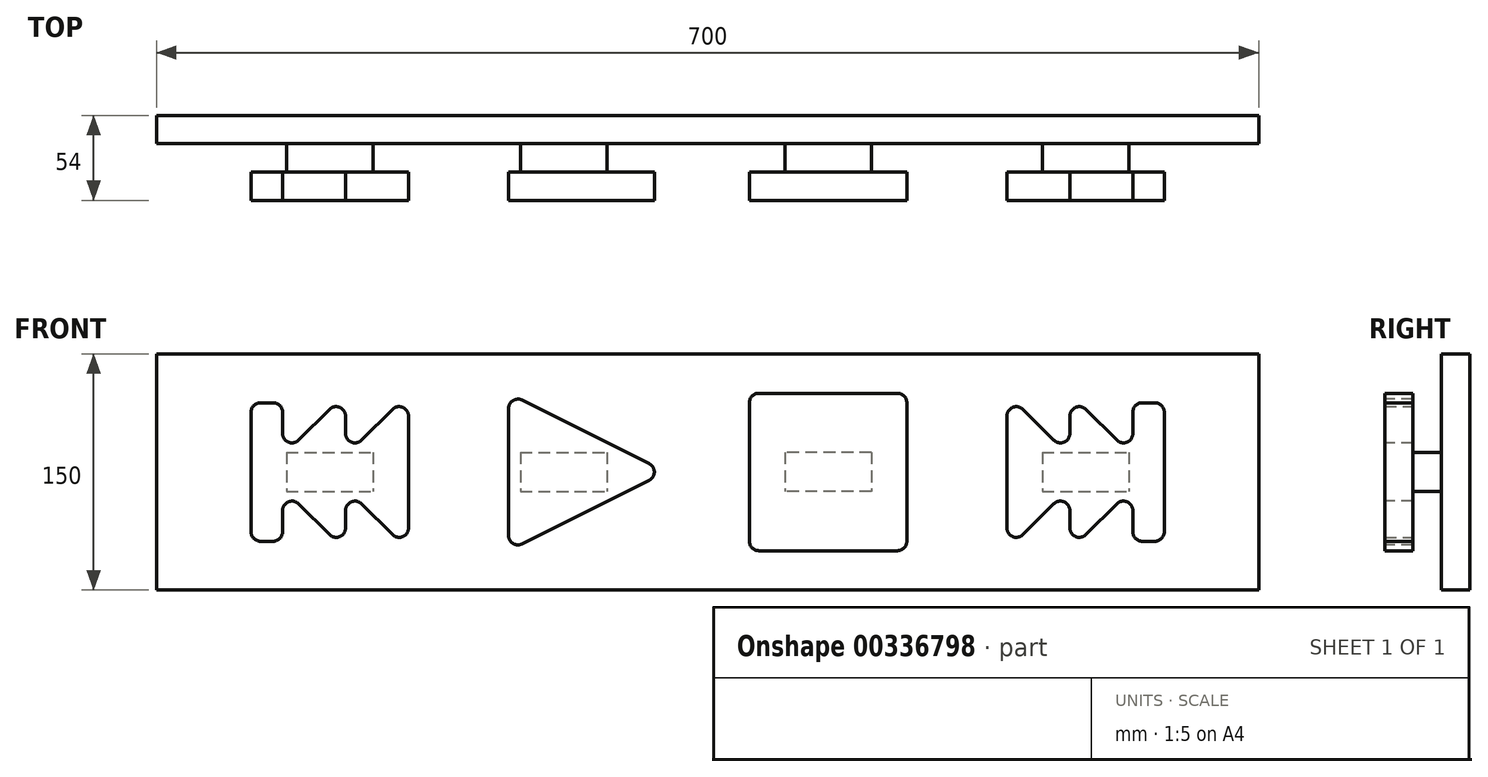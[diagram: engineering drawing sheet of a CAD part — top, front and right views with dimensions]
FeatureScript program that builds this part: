
annotation { "Feature Type Name" : "Feature", "Feature Type Description" : "" }
export const myFeature = defineFeature(function(context is Context, id is Id, definition is map)
    precondition{}
    {
        {
            var Q0;
            Q0=qCreatedBy(makeId("Front.planeOp"),FACE);
            var sketch = newSketch(context, id + "F0", { "sketchPlane" : qUnion([Q0])});
            skLineSegment(sketch, "E0.bottom", {"start": v(350, 75) * mm, "end": v(-350, 75) * mm});
            skLineSegment(sketch, "E0.top", {"start": v(350, -75) * mm, "end": v(-350, -75) * mm});
            skLineSegment(sketch, "E0.left", {"start": v(350, 75) * mm, "end": v(350, -75) * mm});
            skLineSegment(sketch, "E0.right", {"start": v(-350, 75) * mm, "end": v(-350, -75) * mm});
            skPoint(sketch, "E0.middle", {"position": v(0, 0) * mm});
            skSolve(sketch);
        }
        {
            var Q0;
            Q0=makeQuery(id+"F0.imprint","IMPRINT",FACE,{"disambiguationData":[TD([[makeQuery(id+"F0.imprint","IMPRINT",EDGE,{"derivedFrom":sQuery(id+"F0.wireOp",EDGE,"E0.bottom")}),1.0]])]});
            extrude(context, id + "F1", {"entities" : qUnion([Q0]), "depth" : 18 * mm});
        }
        {
            var Q0;
            Q0=makeQuery(id+"F1.opExtrude","CAP_FACE",FACE,{"disambiguationData":[OSD([sQuery(id+"F0.wireOp",EDGE,"E0.bottom"),sQuery(id+"F0.wireOp",EDGE,"E0.top"),sQuery(id+"F0.wireOp",EDGE,"E0.left"),sQuery(id+"F0.wireOp",EDGE,"E0.right")])],"isStart":false});
            var sketch = newSketch(context, id + "F2", { "sketchPlane" : qUnion([Q0])});
            skLineSegment(sketch, "E1.left", {"start": v(50, 50) * mm, "end": v(50, -50) * mm, "construction": true});
            skPoint(sketch, "E1.middle", {"position": v(0, 0) * mm});
            skLineSegment(sketch, "E2", {"start": v(-50, 0) * mm, "end": v(50, 0) * mm, "construction": true});
            skPoint(sketch, "E3", {"position": v(10, 10) * mm});
            skPoint(sketch, "E4", {"position": v(10, -10) * mm});
            skPoint(sketch, "E5", {"position": v(-30, 10) * mm});
            skPoint(sketch, "E6", {"position": v(-30, -10) * mm});
            skLineSegment(sketch, "E7", {"start": v(-50, 44) * mm, "end": v(-50, -44) * mm});
            skLineSegment(sketch, "E8", {"start": v(-30, -44) * mm, "end": v(-30, -10) * mm});
            skLineSegment(sketch, "E9", {"start": v(-30, -10) * mm, "end": v(10, -50) * mm});
            skLineSegment(sketch, "E10", {"start": v(10, -50) * mm, "end": v(10, -10) * mm});
            skLineSegment(sketch, "E11", {"start": v(10, -10) * mm, "end": v(50, -50) * mm});
            skLineSegment(sketch, "E12", {"start": v(50, -50) * mm, "end": v(50, 50) * mm});
            skLineSegment(sketch, "E13", {"start": v(50, 50) * mm, "end": v(10, 10) * mm});
            skLineSegment(sketch, "E14", {"start": v(10, 10) * mm, "end": v(10, 50) * mm});
            skLineSegment(sketch, "E15", {"start": v(10, 50) * mm, "end": v(-30, 10) * mm});
            skLineSegment(sketch, "E16", {"start": v(-30, 10) * mm, "end": v(-30, 44) * mm});
            skLineSegment(sketch, "E17", {"start": v(-50, 44) * mm, "end": v(-30, 44) * mm});
            skLineSegment(sketch, "E18", {"start": v(-50, -44) * mm, "end": v(-30, -44) * mm});
            skPoint(sketch, "E19.orphan", {"position": v(-50, 50) * mm});
            skPoint(sketch, "E20.orphan", {"position": v(-50, -50) * mm});
            skSolve(sketch);
        }
        {
            var Q0;
            Q0 = qSketchRegion(id + "F2", true);
            extrude(context, id + "F3", {"entities" : qUnion([Q0]), "depth" : 18 * mm});
        }
        {
            var Q0;
            Q0=makeQuery(id+"F1.opExtrude","CAP_FACE",FACE,{"disambiguationData":[OSD([sQuery(id+"F0.wireOp",EDGE,"E0.bottom"),sQuery(id+"F0.wireOp",EDGE,"E0.top"),sQuery(id+"F0.wireOp",EDGE,"E0.left"),sQuery(id+"F0.wireOp",EDGE,"E0.right")])],"isStart":false});
            var sketch = newSketch(context, id + "F4", { "sketchPlane" : qUnion([Q0])});
            skLineSegment(sketch, "E21.right", {"start": v(-50, 50) * mm, "end": v(-50, -50) * mm});
            skPoint(sketch, "E21.middle", {"position": v(0, 0) * mm});
            skLineSegment(sketch, "E22", {"start": v(-50, 50) * mm, "end": v(50, 0) * mm});
            skLineSegment(sketch, "E23", {"start": v(50, 0) * mm, "end": v(-50, -50) * mm});
            skSolve(sketch);
        }
        {
            var Q0;
            Q0=makeQuery(id+"F4.imprint","IMPRINT",FACE,{"disambiguationData":[TD([[makeQuery(id+"F4.imprint","IMPRINT",EDGE,{"derivedFrom":sQuery(id+"F4.wireOp",EDGE,"E21.right")}),1.0]])]});
            extrude(context, id + "F5", {"entities" : qUnion([Q0]), "depth" : 18 * mm});
        }
        {
            var Q0;
            Q0=makeQuery(id+"F1.opExtrude","CAP_FACE",FACE,{"disambiguationData":[OSD([sQuery(id+"F0.wireOp",EDGE,"E0.bottom"),sQuery(id+"F0.wireOp",EDGE,"E0.top"),sQuery(id+"F0.wireOp",EDGE,"E0.left"),sQuery(id+"F0.wireOp",EDGE,"E0.right")])],"isStart":false});
            var sketch = newSketch(context, id + "F6", { "sketchPlane" : qUnion([Q0])});
            skLineSegment(sketch, "E24.bottom", {"start": v(50, 50) * mm, "end": v(-50, 50) * mm});
            skLineSegment(sketch, "E24.top", {"start": v(50, -50) * mm, "end": v(-50, -50) * mm});
            skLineSegment(sketch, "E24.left", {"start": v(50, 50) * mm, "end": v(50, -50) * mm});
            skLineSegment(sketch, "E24.right", {"start": v(-50, 50) * mm, "end": v(-50, -50) * mm});
            skPoint(sketch, "E24.middle", {"position": v(0, 0) * mm});
            skSolve(sketch);
        }
        {
            var Q0;
            Q0=makeQuery(id+"F6.imprint","IMPRINT",FACE,{"disambiguationData":[TD([[makeQuery(id+"F6.imprint","IMPRINT",EDGE,{"derivedFrom":sQuery(id+"F6.wireOp",EDGE,"E24.bottom")}),1.0]])]});
            extrude(context, id + "F7", {"entities" : qUnion([Q0]), "depth" : 18 * mm});
        }
        {
            var Q0;
            Q0=makeQuery(id+"F1.opExtrude","CAP_FACE",FACE,{"disambiguationData":[OSD([sQuery(id+"F0.wireOp",EDGE,"E0.bottom"),sQuery(id+"F0.wireOp",EDGE,"E0.top"),sQuery(id+"F0.wireOp",EDGE,"E0.left"),sQuery(id+"F0.wireOp",EDGE,"E0.right")])],"isStart":false});
            var sketch = newSketch(context, id + "F8", { "sketchPlane" : qUnion([Q0])});
            skLineSegment(sketch, "E25.left", {"start": v(-50, -50) * mm, "end": v(-50, 50) * mm, "construction": true});
            skPoint(sketch, "E25.middle", {"position": v(0, 0) * mm});
            skLineSegment(sketch, "E26", {"start": v(50, 0) * mm, "end": v(-50, 0) * mm, "construction": true});
            skPoint(sketch, "E27", {"position": v(-10, -10) * mm});
            skPoint(sketch, "E28", {"position": v(-10, 10) * mm});
            skPoint(sketch, "E29", {"position": v(30, -10) * mm});
            skPoint(sketch, "E30", {"position": v(30, 10) * mm});
            skLineSegment(sketch, "E31", {"start": v(50, -44) * mm, "end": v(50, 44) * mm});
            skLineSegment(sketch, "E32", {"start": v(30, 44) * mm, "end": v(30, 10) * mm});
            skLineSegment(sketch, "E33", {"start": v(30, 10) * mm, "end": v(-10, 50) * mm});
            skLineSegment(sketch, "E34", {"start": v(-10, 50) * mm, "end": v(-10, 10) * mm});
            skLineSegment(sketch, "E35", {"start": v(-10, 10) * mm, "end": v(-50, 50) * mm});
            skLineSegment(sketch, "E36", {"start": v(-50, 50) * mm, "end": v(-50, -50) * mm});
            skLineSegment(sketch, "E37", {"start": v(-50, -50) * mm, "end": v(-10, -10) * mm});
            skLineSegment(sketch, "E38", {"start": v(-10, -10) * mm, "end": v(-10, -50) * mm});
            skLineSegment(sketch, "E39", {"start": v(-10, -50) * mm, "end": v(30, -10) * mm});
            skLineSegment(sketch, "E40", {"start": v(30, -10) * mm, "end": v(30, -44) * mm});
            skLineSegment(sketch, "E41", {"start": v(30, 44) * mm, "end": v(50, 44) * mm});
            skLineSegment(sketch, "E42", {"start": v(30, -44) * mm, "end": v(50, -44) * mm});
            skPoint(sketch, "E43.orphan", {"position": v(50, 50) * mm});
            skPoint(sketch, "E44.end.orphan", {"position": v(50, -50) * mm});
            skSolve(sketch);
        }
        {
            var Q0;
            Q0=makeQuery(id+"F8.imprint","IMPRINT",FACE,{"disambiguationData":[TD([[makeQuery(id+"F8.imprint","IMPRINT",EDGE,{"derivedFrom":sQuery(id+"F8.wireOp",EDGE,"E31")}),1.0]])]});
            extrude(context, id + "F9", {"entities" : qUnion([Q0]), "depth" : 18 * mm});
        }
        {
            var Q0;
            Q0=makeQuery(id+"F3.opExtrude","SWEPT_EDGE",EDGE,{"disambiguationData":[OSD([sQuery(id+"F2.wireOp",EDGE,"jNEnzam2-YLTJ-LkkW-kFy7-VWHj9kg6MtIO"),sQuery(id+"F2.wireOp",EDGE,"E7")])]});
            var Q1;
            Q1=makeQuery(id+"F3.opExtrude","SWEPT_EDGE",EDGE,{"disambiguationData":[OSD([sQuery(id+"F2.wireOp",EDGE,"jNEnzam2-YLTJ-LkkW-kFy7-VWHj9kg6MtIO"),sQuery(id+"F2.wireOp",EDGE,"E16")])]});
            var Q2;
            Q2=makeQuery(id+"F3.opExtrude","SWEPT_EDGE",EDGE,{"disambiguationData":[OSD([sQuery(id+"F2.wireOp",EDGE,"E14"),sQuery(id+"F2.wireOp",EDGE,"E15")])]});
            var Q3;
            Q3=makeQuery(id+"F3.opExtrude","SWEPT_EDGE",EDGE,{"disambiguationData":[OSD([sQuery(id+"F2.wireOp",EDGE,"E12"),sQuery(id+"F2.wireOp",EDGE,"E13")])]});
            var Q4;
            Q4=makeQuery(id+"F5.opExtrude","SWEPT_EDGE",EDGE,{"disambiguationData":[OSD([sQuery(id+"F4.wireOp",EDGE,"E21.right"),sQuery(id+"F4.wireOp",EDGE,"E22")])]});
            var Q5;
            Q5=makeQuery(id+"F7.opExtrude","SWEPT_EDGE",EDGE,{"disambiguationData":[OSD([sQuery(id+"F6.wireOp",EDGE,"E24.bottom"),sQuery(id+"F6.wireOp",EDGE,"E24.right")])]});
            var Q6;
            Q6=makeQuery(id+"F7.opExtrude","SWEPT_EDGE",EDGE,{"disambiguationData":[OSD([sQuery(id+"F6.wireOp",EDGE,"E24.bottom"),sQuery(id+"F6.wireOp",EDGE,"E24.left")])]});
            var Q7;
            Q7=makeQuery(id+"F3.opExtrude","SWEPT_EDGE",EDGE,{"disambiguationData":[OSD([sQuery(id+"F2.wireOp",EDGE,"E15"),sQuery(id+"F2.wireOp",EDGE,"E16")])]});
            var Q8;
            Q8=makeQuery(id+"F3.opExtrude","SWEPT_EDGE",EDGE,{"disambiguationData":[OSD([sQuery(id+"F2.wireOp",EDGE,"E13"),sQuery(id+"F2.wireOp",EDGE,"E14")])]});
            var Q9;
            Q9=makeQuery(id+"F7.opExtrude","SWEPT_EDGE",EDGE,{"disambiguationData":[OSD([sQuery(id+"F6.wireOp",EDGE,"E24.top"),sQuery(id+"F6.wireOp",EDGE,"E24.left")])]});
            var Q10;
            Q10=makeQuery(id+"F7.opExtrude","SWEPT_EDGE",EDGE,{"disambiguationData":[OSD([sQuery(id+"F6.wireOp",EDGE,"E24.top"),sQuery(id+"F6.wireOp",EDGE,"E24.right")])]});
            var Q11;
            Q11=makeQuery(id+"F5.opExtrude","SWEPT_EDGE",EDGE,{"disambiguationData":[OSD([sQuery(id+"F4.wireOp",EDGE,"E22"),sQuery(id+"F4.wireOp",EDGE,"E23")])]});
            var Q12;
            Q12=makeQuery(id+"F5.opExtrude","SWEPT_EDGE",EDGE,{"disambiguationData":[OSD([sQuery(id+"F4.wireOp",EDGE,"E21.right"),sQuery(id+"F4.wireOp",EDGE,"E23")])]});
            var Q13;
            Q13=makeQuery(id+"F3.opExtrude","SWEPT_EDGE",EDGE,{"disambiguationData":[OSD([sQuery(id+"F2.wireOp",EDGE,"E11"),sQuery(id+"F2.wireOp",EDGE,"E12")])]});
            var Q14;
            Q14=makeQuery(id+"F3.opExtrude","SWEPT_EDGE",EDGE,{"disambiguationData":[OSD([sQuery(id+"F2.wireOp",EDGE,"E9"),sQuery(id+"F2.wireOp",EDGE,"E10")])]});
            var Q15;
            Q15=makeQuery(id+"F3.opExtrude","SWEPT_EDGE",EDGE,{"disambiguationData":[OSD([sQuery(id+"F2.wireOp",EDGE,"ZUAhIKnp-DANw-6E52-ARa7-giLd2jf8w72K"),sQuery(id+"F2.wireOp",EDGE,"E8")])]});
            var Q16;
            Q16=makeQuery(id+"F3.opExtrude","SWEPT_EDGE",EDGE,{"disambiguationData":[OSD([sQuery(id+"F2.wireOp",EDGE,"E7"),sQuery(id+"F2.wireOp",EDGE,"ZUAhIKnp-DANw-6E52-ARa7-giLd2jf8w72K")])]});
            var Q17;
            Q17=makeQuery(id+"F3.opExtrude","SWEPT_EDGE",EDGE,{"disambiguationData":[OSD([sQuery(id+"F2.wireOp",EDGE,"E10"),sQuery(id+"F2.wireOp",EDGE,"E11")])]});
            var Q18;
            Q18=makeQuery(id+"F3.opExtrude","SWEPT_EDGE",EDGE,{"disambiguationData":[OSD([sQuery(id+"F2.wireOp",EDGE,"E8"),sQuery(id+"F2.wireOp",EDGE,"E9")])]});
            var Q19;
            Q19=makeQuery(id+"F9.opExtrude","SWEPT_EDGE",EDGE,{"disambiguationData":[OSD([sQuery(id+"F8.wireOp",EDGE,"E32"),sQuery(id+"F8.wireOp",EDGE,"E41")])]});
            var Q20;
            Q20=makeQuery(id+"F9.opExtrude","SWEPT_EDGE",EDGE,{"disambiguationData":[OSD([sQuery(id+"F8.wireOp",EDGE,"E31"),sQuery(id+"F8.wireOp",EDGE,"E41")])]});
            var Q21;
            Q21=makeQuery(id+"F9.opExtrude","SWEPT_EDGE",EDGE,{"disambiguationData":[OSD([sQuery(id+"F8.wireOp",EDGE,"E31"),sQuery(id+"F8.wireOp",EDGE,"E42")])]});
            var Q22;
            Q22=makeQuery(id+"F9.opExtrude","SWEPT_EDGE",EDGE,{"disambiguationData":[OSD([sQuery(id+"F8.wireOp",EDGE,"E40"),sQuery(id+"F8.wireOp",EDGE,"E42")])]});
            var Q23;
            Q23=makeQuery(id+"F9.opExtrude","SWEPT_EDGE",EDGE,{"disambiguationData":[OSD([sQuery(id+"F8.wireOp",EDGE,"E33"),sQuery(id+"F8.wireOp",EDGE,"E34")])]});
            var Q24;
            Q24=makeQuery(id+"F9.opExtrude","SWEPT_EDGE",EDGE,{"disambiguationData":[OSD([sQuery(id+"F8.wireOp",EDGE,"E35"),sQuery(id+"F8.wireOp",EDGE,"E36")])]});
            var Q25;
            Q25=makeQuery(id+"F9.opExtrude","SWEPT_EDGE",EDGE,{"disambiguationData":[OSD([sQuery(id+"F8.wireOp",EDGE,"E38"),sQuery(id+"F8.wireOp",EDGE,"E39")])]});
            var Q26;
            Q26=makeQuery(id+"F9.opExtrude","SWEPT_EDGE",EDGE,{"disambiguationData":[OSD([sQuery(id+"F8.wireOp",EDGE,"E36"),sQuery(id+"F8.wireOp",EDGE,"E37")])]});
            var Q27;
            Q27=makeQuery(id+"F9.opExtrude","SWEPT_EDGE",EDGE,{"disambiguationData":[OSD([sQuery(id+"F8.wireOp",EDGE,"E34"),sQuery(id+"F8.wireOp",EDGE,"E35")])]});
            var Q28;
            Q28=makeQuery(id+"F9.opExtrude","SWEPT_EDGE",EDGE,{"disambiguationData":[OSD([sQuery(id+"F8.wireOp",EDGE,"E32"),sQuery(id+"F8.wireOp",EDGE,"E33")])]});
            var Q29;
            Q29=makeQuery(id+"F9.opExtrude","SWEPT_EDGE",EDGE,{"disambiguationData":[OSD([sQuery(id+"F8.wireOp",EDGE,"E39"),sQuery(id+"F8.wireOp",EDGE,"E40")])]});
            var Q30;
            Q30=makeQuery(id+"F9.opExtrude","SWEPT_EDGE",EDGE,{"disambiguationData":[OSD([sQuery(id+"F8.wireOp",EDGE,"E37"),sQuery(id+"F8.wireOp",EDGE,"E38")])]});
            fillet(context, id + "F10", {"entities" : qUnion([Q0, Q1, Q2, Q3, Q4, Q5, Q6, Q7, Q8, Q9, Q10, Q11, Q12, Q13, Q14, Q15, Q16, Q17, Q18, Q19, Q20, Q21, Q22, Q23, Q24, Q25, Q26, Q27, Q28, Q29, Q30]), "radius" : 6 * mm, "tangentPropagation" : true, "allowEdgeOverflow" : false});
        }
        {
            var Q0;
            Q0=makeQuery(id+"F3.opExtrude","SWEPT_BODY",BODY,{"disambiguationData":[OSD([sQuery(id+"F2.wireOp",EDGE,"E7"),sQuery(id+"F2.wireOp",EDGE,"E8"),sQuery(id+"F2.wireOp",EDGE,"E9"),sQuery(id+"F2.wireOp",EDGE,"E10"),sQuery(id+"F2.wireOp",EDGE,"E11"),sQuery(id+"F2.wireOp",EDGE,"E12"),sQuery(id+"F2.wireOp",EDGE,"E13"),sQuery(id+"F2.wireOp",EDGE,"E14"),sQuery(id+"F2.wireOp",EDGE,"E15"),sQuery(id+"F2.wireOp",EDGE,"E16"),sQuery(id+"F2.wireOp",EDGE,"E17"),sQuery(id+"F2.wireOp",EDGE,"E18")])]});
            transform(context, id + "F11", {"entities" : qUnion([Q0]), "transformType" : TransformType.TRANSLATION_3D, "dx" : -240 * mm, "dy" : 0 * mm, "dz" : 0 * mm, "makeCopy" : false});
        }
        {
            var Q0;
            Q0=makeQuery(id+"F5.opExtrude","SWEPT_BODY",BODY,{"disambiguationData":[OSD([sQuery(id+"F4.wireOp",EDGE,"E21.right"),sQuery(id+"F4.wireOp",EDGE,"E22"),sQuery(id+"F4.wireOp",EDGE,"E23")])]});
            transform(context, id + "F12", {"entities" : qUnion([Q0]), "transformType" : TransformType.TRANSLATION_3D, "dx" : -80 * mm, "dy" : 0 * mm, "dz" : 0 * mm, "makeCopy" : false});
        }
        {
            var Q0;
            Q0=makeQuery(id+"F9.opExtrude","SWEPT_BODY",BODY,{"disambiguationData":[OSD([sQuery(id+"F8.wireOp",EDGE,"E31"),sQuery(id+"F8.wireOp",EDGE,"E32"),sQuery(id+"F8.wireOp",EDGE,"E33"),sQuery(id+"F8.wireOp",EDGE,"E34"),sQuery(id+"F8.wireOp",EDGE,"E35"),sQuery(id+"F8.wireOp",EDGE,"E36"),sQuery(id+"F8.wireOp",EDGE,"E37"),sQuery(id+"F8.wireOp",EDGE,"E38"),sQuery(id+"F8.wireOp",EDGE,"E39"),sQuery(id+"F8.wireOp",EDGE,"E40"),sQuery(id+"F8.wireOp",EDGE,"E41"),sQuery(id+"F8.wireOp",EDGE,"E42")])]});
            transform(context, id + "F13", {"entities" : qUnion([Q0]), "transformType" : TransformType.TRANSLATION_3D, "dx" : 240 * mm, "dy" : 0 * mm, "dz" : 0 * mm, "makeCopy" : false});
        }
        {
            var Q0;
            Q0=makeQuery(id+"F7.opExtrude","SWEPT_BODY",BODY,{"disambiguationData":[OSD([sQuery(id+"F6.wireOp",EDGE,"E24.bottom"),sQuery(id+"F6.wireOp",EDGE,"E24.top"),sQuery(id+"F6.wireOp",EDGE,"E24.left"),sQuery(id+"F6.wireOp",EDGE,"E24.right")])]});
            transform(context, id + "F14", {"entities" : qUnion([Q0]), "transformType" : TransformType.TRANSLATION_3D, "dx" : 80 * mm, "dy" : 0 * mm, "dz" : 0 * mm, "makeCopy" : false});
        }
        {
            var Q0;
            Q0=makeQuery(id+"F7.opExtrude","SWEPT_BODY",BODY,{"disambiguationData":[OSD([sQuery(id+"F6.wireOp",EDGE,"E24.bottom"),sQuery(id+"F6.wireOp",EDGE,"E24.top"),sQuery(id+"F6.wireOp",EDGE,"E24.left"),sQuery(id+"F6.wireOp",EDGE,"E24.right")])]});
            transform(context, id + "F15", {"entities" : qUnion([Q0]), "transformType" : TransformType.TRANSLATION_3D, "dx" : -3.5 * mm, "dy" : 0 * mm, "dz" : 0 * mm, "makeCopy" : false});
        }
        {
            var Q0;
            Q0=makeQuery(id+"F5.opExtrude","SWEPT_BODY",BODY,{"disambiguationData":[OSD([sQuery(id+"F4.wireOp",EDGE,"E21.right"),sQuery(id+"F4.wireOp",EDGE,"E22"),sQuery(id+"F4.wireOp",EDGE,"E23")])]});
            transform(context, id + "F16", {"entities" : qUnion([Q0]), "transformType" : TransformType.TRANSLATION_3D, "dx" : 3.5 * mm, "dy" : 0 * mm, "dz" : 0 * mm, "makeCopy" : false});
        }
        {
            var Q0;
            Q0=makeQuery(id+"F3.opExtrude","SWEPT_BODY",BODY,{"disambiguationData":[OSD([sQuery(id+"F2.wireOp",EDGE,"E7"),sQuery(id+"F2.wireOp",EDGE,"E8"),sQuery(id+"F2.wireOp",EDGE,"E9"),sQuery(id+"F2.wireOp",EDGE,"E10"),sQuery(id+"F2.wireOp",EDGE,"E11"),sQuery(id+"F2.wireOp",EDGE,"E12"),sQuery(id+"F2.wireOp",EDGE,"E13"),sQuery(id+"F2.wireOp",EDGE,"E14"),sQuery(id+"F2.wireOp",EDGE,"E15"),sQuery(id+"F2.wireOp",EDGE,"E16"),sQuery(id+"F2.wireOp",EDGE,"E17"),sQuery(id+"F2.wireOp",EDGE,"E18")])]});
            var Q1;
            Q1=makeQuery(id+"F5.opExtrude","SWEPT_BODY",BODY,{"disambiguationData":[OSD([sQuery(id+"F4.wireOp",EDGE,"E21.right"),sQuery(id+"F4.wireOp",EDGE,"E22"),sQuery(id+"F4.wireOp",EDGE,"E23")])]});
            var Q2;
            Q2=makeQuery(id+"F7.opExtrude","SWEPT_BODY",BODY,{"disambiguationData":[OSD([sQuery(id+"F6.wireOp",EDGE,"E24.bottom"),sQuery(id+"F6.wireOp",EDGE,"E24.top"),sQuery(id+"F6.wireOp",EDGE,"E24.left"),sQuery(id+"F6.wireOp",EDGE,"E24.right")])]});
            var Q3;
            Q3=makeQuery(id+"F9.opExtrude","SWEPT_BODY",BODY,{"disambiguationData":[OSD([sQuery(id+"F8.wireOp",EDGE,"E31"),sQuery(id+"F8.wireOp",EDGE,"E32"),sQuery(id+"F8.wireOp",EDGE,"E33"),sQuery(id+"F8.wireOp",EDGE,"E34"),sQuery(id+"F8.wireOp",EDGE,"E35"),sQuery(id+"F8.wireOp",EDGE,"E36"),sQuery(id+"F8.wireOp",EDGE,"E37"),sQuery(id+"F8.wireOp",EDGE,"E38"),sQuery(id+"F8.wireOp",EDGE,"E39"),sQuery(id+"F8.wireOp",EDGE,"E40"),sQuery(id+"F8.wireOp",EDGE,"E41"),sQuery(id+"F8.wireOp",EDGE,"E42")])]});
            transform(context, id + "F17", {"entities" : qUnion([Q0, Q1, Q2, Q3]), "transformType" : TransformType.TRANSLATION_3D, "dx" : 0 * mm, "dy" : -18 * mm, "dz" : 0 * mm, "makeCopy" : false});
        }
        {
            var Q0;
            Q0=makeQuery(id+"F1.opExtrude","CAP_FACE",FACE,{"disambiguationData":[OSD([sQuery(id+"F0.wireOp",EDGE,"E0.bottom"),sQuery(id+"F0.wireOp",EDGE,"E0.top"),sQuery(id+"F0.wireOp",EDGE,"E0.left"),sQuery(id+"F0.wireOp",EDGE,"E0.right")])],"isStart":false});
            var sketch = newSketch(context, id + "F18", { "sketchPlane" : qUnion([Q0])});
            skLineSegment(sketch, "E45.0.0", {"start": v(-270, 24.49) * mm, "end": v(-270, 38) * mm, "construction": true});
            skArc(sketch, "E45.0.1", {"start": v(-270, 38) * mm, "mid": v(-271.76, 42.24) * mm, "end": v(-276, 44) * mm, "construction": true});
            skLineSegment(sketch, "E45.0.2", {"start": v(-276, 44) * mm, "end": v(-284, 44) * mm, "construction": true});
            skArc(sketch, "E45.0.3", {"start": v(-284, 44) * mm, "mid": v(-288.24, 42.24) * mm, "end": v(-290, 38) * mm, "construction": true});
            skLineSegment(sketch, "E45.0.4", {"start": v(-290, 38) * mm, "end": v(-290, -38) * mm, "construction": true});
            skArc(sketch, "E45.0.5", {"start": v(-290, -38) * mm, "mid": v(-288.24, -42.24) * mm, "end": v(-284, -44) * mm, "construction": true});
            skLineSegment(sketch, "E45.0.6", {"start": v(-284, -44) * mm, "end": v(-276, -44) * mm, "construction": true});
            skArc(sketch, "E45.0.7", {"start": v(-276, -44) * mm, "mid": v(-271.76, -42.24) * mm, "end": v(-270, -38) * mm, "construction": true});
            skLineSegment(sketch, "E45.0.8", {"start": v(-270, -38) * mm, "end": v(-270, -24.49) * mm, "construction": true});
            skArc(sketch, "E45.0.9", {"start": v(-270, -24.49) * mm, "mid": v(-266.3, -18.94) * mm, "end": v(-259.76, -20.24) * mm, "construction": true});
            skLineSegment(sketch, "E45.0.10", {"start": v(-259.76, -20.24) * mm, "end": v(-240.24, -39.76) * mm, "construction": true});
            skArc(sketch, "E45.0.11", {"start": v(-240.24, -39.76) * mm, "mid": v(-233.7, -41.06) * mm, "end": v(-230, -35.51) * mm, "construction": true});
            skLineSegment(sketch, "E45.0.12", {"start": v(-230, -35.51) * mm, "end": v(-230, -24.49) * mm, "construction": true});
            skArc(sketch, "E45.0.13", {"start": v(-230, -24.49) * mm, "mid": v(-226.3, -18.94) * mm, "end": v(-219.76, -20.24) * mm, "construction": true});
            skLineSegment(sketch, "E45.0.14", {"start": v(-219.76, -20.24) * mm, "end": v(-200.24, -39.76) * mm, "construction": true});
            skArc(sketch, "E45.0.15", {"start": v(-200.24, -39.76) * mm, "mid": v(-193.7, -41.06) * mm, "end": v(-190, -35.51) * mm, "construction": true});
            skLineSegment(sketch, "E45.0.16", {"start": v(-190, -35.51) * mm, "end": v(-190, 35.51) * mm, "construction": true});
            skArc(sketch, "E45.0.17", {"start": v(-190, 35.51) * mm, "mid": v(-193.7, 41.06) * mm, "end": v(-200.24, 39.76) * mm, "construction": true});
            skLineSegment(sketch, "E45.0.18", {"start": v(-200.24, 39.76) * mm, "end": v(-219.76, 20.24) * mm, "construction": true});
            skArc(sketch, "E45.0.19", {"start": v(-219.76, 20.24) * mm, "mid": v(-226.3, 18.94) * mm, "end": v(-230, 24.49) * mm, "construction": true});
            skLineSegment(sketch, "E45.0.20", {"start": v(-230, 24.49) * mm, "end": v(-230, 35.51) * mm, "construction": true});
            skArc(sketch, "E45.0.21", {"start": v(-230, 35.51) * mm, "mid": v(-233.7, 41.06) * mm, "end": v(-240.24, 39.76) * mm, "construction": true});
            skLineSegment(sketch, "E45.0.22", {"start": v(-240.24, 39.76) * mm, "end": v(-259.76, 20.24) * mm, "construction": true});
            skArc(sketch, "E45.0.23", {"start": v(-259.76, 20.24) * mm, "mid": v(-266.3, 18.94) * mm, "end": v(-270, 24.49) * mm, "construction": true});
            skLineSegment(sketch, "E45.1.0", {"start": v(-117.82, -45.66) * mm, "end": v(-37.23, -5.37) * mm, "construction": true});
            skArc(sketch, "E45.1.1", {"start": v(-37.23, -5.37) * mm, "mid": v(-33.92, 0) * mm, "end": v(-37.23, 5.37) * mm, "construction": true});
            skLineSegment(sketch, "E45.1.2", {"start": v(-37.23, 5.37) * mm, "end": v(-117.82, 45.66) * mm, "construction": true});
            skArc(sketch, "E45.1.3", {"start": v(-117.82, 45.66) * mm, "mid": v(-123.65, 45.4) * mm, "end": v(-126.5, 40.3) * mm, "construction": true});
            skLineSegment(sketch, "E45.1.4", {"start": v(-126.5, 40.3) * mm, "end": v(-126.5, -40.3) * mm, "construction": true});
            skArc(sketch, "E45.1.5", {"start": v(-126.5, -40.3) * mm, "mid": v(-123.65, -45.4) * mm, "end": v(-117.82, -45.66) * mm, "construction": true});
            skLineSegment(sketch, "E45.2.0", {"start": v(32.5, -50) * mm, "end": v(120.5, -50) * mm, "construction": true});
            skArc(sketch, "E45.2.1", {"start": v(120.5, -50) * mm, "mid": v(124.74, -48.24) * mm, "end": v(126.5, -44) * mm, "construction": true});
            skLineSegment(sketch, "E45.2.2", {"start": v(126.5, -44) * mm, "end": v(126.5, 44) * mm, "construction": true});
            skArc(sketch, "E45.2.3", {"start": v(126.5, 44) * mm, "mid": v(124.74, 48.24) * mm, "end": v(120.5, 50) * mm, "construction": true});
            skLineSegment(sketch, "E45.2.4", {"start": v(120.5, 50) * mm, "end": v(32.5, 50) * mm, "construction": true});
            skArc(sketch, "E45.2.5", {"start": v(32.5, 50) * mm, "mid": v(28.26, 48.24) * mm, "end": v(26.5, 44) * mm, "construction": true});
            skLineSegment(sketch, "E45.2.6", {"start": v(26.5, 44) * mm, "end": v(26.5, -44) * mm, "construction": true});
            skArc(sketch, "E45.2.7", {"start": v(26.5, -44) * mm, "mid": v(28.26, -48.24) * mm, "end": v(32.5, -50) * mm, "construction": true});
            skLineSegment(sketch, "E45.3.0", {"start": v(270, -24.49) * mm, "end": v(270, -38) * mm, "construction": true});
            skArc(sketch, "E45.3.1", {"start": v(270, -38) * mm, "mid": v(271.76, -42.24) * mm, "end": v(276, -44) * mm, "construction": true});
            skLineSegment(sketch, "E45.3.2", {"start": v(276, -44) * mm, "end": v(284, -44) * mm, "construction": true});
            skArc(sketch, "E45.3.3", {"start": v(284, -44) * mm, "mid": v(288.24, -42.24) * mm, "end": v(290, -38) * mm, "construction": true});
            skLineSegment(sketch, "E45.3.4", {"start": v(290, -38) * mm, "end": v(290, 38) * mm, "construction": true});
            skArc(sketch, "E45.3.5", {"start": v(290, 38) * mm, "mid": v(288.24, 42.24) * mm, "end": v(284, 44) * mm, "construction": true});
            skLineSegment(sketch, "E45.3.6", {"start": v(284, 44) * mm, "end": v(276, 44) * mm, "construction": true});
            skArc(sketch, "E45.3.7", {"start": v(276, 44) * mm, "mid": v(271.76, 42.24) * mm, "end": v(270, 38) * mm, "construction": true});
            skLineSegment(sketch, "E45.3.8", {"start": v(270, 38) * mm, "end": v(270, 24.49) * mm, "construction": true});
            skArc(sketch, "E45.3.9", {"start": v(270, 24.49) * mm, "mid": v(266.3, 18.94) * mm, "end": v(259.76, 20.24) * mm, "construction": true});
            skLineSegment(sketch, "E45.3.10", {"start": v(259.76, 20.24) * mm, "end": v(240.24, 39.76) * mm, "construction": true});
            skArc(sketch, "E45.3.11", {"start": v(240.24, 39.76) * mm, "mid": v(233.7, 41.06) * mm, "end": v(230, 35.51) * mm, "construction": true});
            skLineSegment(sketch, "E45.3.12", {"start": v(230, 35.51) * mm, "end": v(230, 24.49) * mm, "construction": true});
            skArc(sketch, "E45.3.13", {"start": v(230, 24.49) * mm, "mid": v(226.3, 18.94) * mm, "end": v(219.76, 20.24) * mm, "construction": true});
            skLineSegment(sketch, "E45.3.14", {"start": v(219.76, 20.24) * mm, "end": v(200.24, 39.76) * mm, "construction": true});
            skArc(sketch, "E45.3.15", {"start": v(200.24, 39.76) * mm, "mid": v(193.7, 41.06) * mm, "end": v(190, 35.51) * mm, "construction": true});
            skLineSegment(sketch, "E45.3.16", {"start": v(190, 35.51) * mm, "end": v(190, -35.51) * mm, "construction": true});
            skArc(sketch, "E45.3.17", {"start": v(190, -35.51) * mm, "mid": v(193.7, -41.06) * mm, "end": v(200.24, -39.76) * mm, "construction": true});
            skLineSegment(sketch, "E45.3.18", {"start": v(200.24, -39.76) * mm, "end": v(219.76, -20.24) * mm, "construction": true});
            skArc(sketch, "E45.3.19", {"start": v(219.76, -20.24) * mm, "mid": v(226.3, -18.94) * mm, "end": v(230, -24.49) * mm, "construction": true});
            skLineSegment(sketch, "E45.3.20", {"start": v(230, -24.49) * mm, "end": v(230, -35.51) * mm, "construction": true});
            skArc(sketch, "E45.3.21", {"start": v(230, -35.51) * mm, "mid": v(233.7, -41.06) * mm, "end": v(240.24, -39.76) * mm, "construction": true});
            skLineSegment(sketch, "E45.3.22", {"start": v(240.24, -39.76) * mm, "end": v(259.76, -20.24) * mm, "construction": true});
            skArc(sketch, "E45.3.23", {"start": v(259.76, -20.24) * mm, "mid": v(266.3, -18.94) * mm, "end": v(270, -24.49) * mm, "construction": true});
            skLineSegment(sketch, "E46", {"start": v(-350, 0) * mm, "end": v(350, 0) * mm, "construction": true});
            skLineSegment(sketch, "E47.bottom", {"start": v(104, 12.5) * mm, "end": v(49, 12.5) * mm});
            skLineSegment(sketch, "E47.top", {"start": v(104, -12.5) * mm, "end": v(49, -12.5) * mm});
            skLineSegment(sketch, "E47.left", {"start": v(104, 12.5) * mm, "end": v(104, -12.5) * mm});
            skLineSegment(sketch, "E47.right", {"start": v(49, 12.5) * mm, "end": v(49, -12.5) * mm});
            skPoint(sketch, "E47.middle", {"position": v(76.5, 0) * mm});
            skLineSegment(sketch, "E48.bottom", {"start": v(-119, 12.5) * mm, "end": v(-64, 12.5) * mm});
            skLineSegment(sketch, "E48.top", {"start": v(-119, -12.5) * mm, "end": v(-64, -12.5) * mm});
            skLineSegment(sketch, "E48.left", {"start": v(-119, 12.5) * mm, "end": v(-119, -12.5) * mm});
            skLineSegment(sketch, "E48.right", {"start": v(-64, 12.5) * mm, "end": v(-64, -12.5) * mm});
            skPoint(sketch, "E48.middle", {"position": v(-91.5, 0) * mm});
            skLineSegment(sketch, "E49.bottom", {"start": v(-267.5, 12.5) * mm, "end": v(-212.5, 12.5) * mm});
            skLineSegment(sketch, "E49.top", {"start": v(-267.5, -12.5) * mm, "end": v(-212.5, -12.5) * mm});
            skLineSegment(sketch, "E49.left", {"start": v(-267.5, 12.5) * mm, "end": v(-267.5, -12.5) * mm});
            skLineSegment(sketch, "E49.right", {"start": v(-212.5, 12.5) * mm, "end": v(-212.5, -12.5) * mm});
            skPoint(sketch, "E49.middle", {"position": v(-240, 0) * mm});
            skLineSegment(sketch, "E50.bottom", {"start": v(212.5, 12.5) * mm, "end": v(267.5, 12.5) * mm});
            skLineSegment(sketch, "E50.top", {"start": v(212.5, -12.5) * mm, "end": v(267.5, -12.5) * mm});
            skLineSegment(sketch, "E50.left", {"start": v(212.5, 12.5) * mm, "end": v(212.5, -12.5) * mm});
            skLineSegment(sketch, "E50.right", {"start": v(267.5, 12.5) * mm, "end": v(267.5, -12.5) * mm});
            skPoint(sketch, "E50.middle", {"position": v(240, 0) * mm});
            skSolve(sketch);
        }
        {
            var Q0;
            Q0 = qSketchRegion(id + "F18", true);
            extrude(context, id + "F19", {"entities" : qUnion([Q0]), "depth" : 18 * mm});
        }
    });
